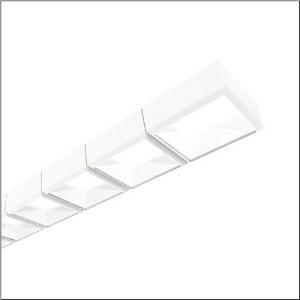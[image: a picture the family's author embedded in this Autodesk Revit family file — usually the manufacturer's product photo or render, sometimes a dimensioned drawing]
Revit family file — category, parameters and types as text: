
# Revit family: scriptus_r__11_5mz314d04wa_e059
name_source: partatom
category: Lighting Fixtures
units: mm (PartAtom-declared; Revit-internal decimal feet)

## family parameters
Cut with Voids When Loaded = No
Host = Face
Light Source = No
Part Type = Normal
Room Calculation Point = No
Round Connector Dimension = Use Diameter
Shared = No

## types (1)
- Scriptus® 11 (1 x LED 4000K / CRI = 80 (unbekannt), 3220 lm / 4820 lm, 4000K)
    Apparent Load = 120 VA
    CIE Flux Codes = - - - 0 100 / 82 95 99 100 100
    Color Rendering = 80
    Color Temperature = 4000K
    Default Elevation = 1800 mm
    Description = Scriptus® 11, office luminaire, primary optical cover: lenses, CAT 2 (L<= 3000cd/m²), light emission: direct/indirect distribution, primary light characteristic: symmetric, installation type: suspended mounting, LED, rated luminous flux: 16.060lm, luminous efficacy: 133lm/W, light colour: 840, colour temperature: 4000K, control gear: DALI, with terminal, 5-pole, mains connection: 230V, AC, 50Hz, rated input power: 120W, LED, control gear: ECG DALI, housing, luminaire housing, of aluminium, traffic white (RAL 9016), length: 3.088mm, width: 114mm, height: 57mm, protection rating (complete): IP20, insulation class (complete): insulation class I (protective earthing), certification: CE, ENEC, VDE, protection symbol: F, permissible operating ambient temperature: 0..+35°C, standard: EN 50419, packaging unit: 1 piece
    Height = 57 mm
    Lamp = 1 x LED 4000K / CRI >= 80 (unbekannt)
    Lamp Light Flux = 3220 lm / 4820 lm
    Lamp count = 1
    Length = 3088 mm
    Luminous efficacy = 134 lm/W
    Manufacturer = Siteco
    ModVariant = No
    Model = 5MZ314D04WA
    Mounting Place = Ceiling
    Mounting Type = Pendant
    Number of Poles = 1
    OnlyDefault = Yes
    Power Factor = 1
    Product Name = Scriptus® 11
    Product group = office luminaire | ceiling pendant
    ProductGroupID = 903
    Protection Class = Protection class I
    Protection Degree = IP 20
    RLX_Detail_Level = 1
    RLX_Emergency_Light_Flux = 0 lm
    RLX_Emergency_Type = 0
    RLX_Emergency_Type_DB = No
    RlxData = <blob elided: 31977 chars, md5=f3a9c551>
    Socket = socket
    Standby Power = 0 W
    System Light Flux = 16080 lm
    System Power = 120 W
    Type Comments = Product without accessories
    Type Image = l_1004839.jpg
    URL = http://relux.com
    VarID = ---
    Voltage = 0 V
    Weight = 0.00 kg
    Width = 114 mm

## geometry (parser evidence)
native form markers: Blend x4, Sweep x19
no freeform markers — native parametric forms only
